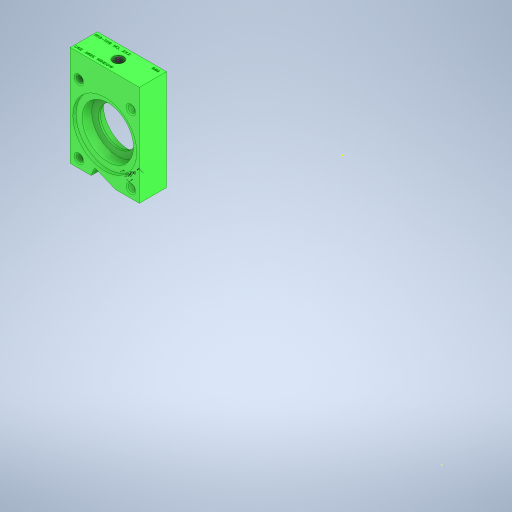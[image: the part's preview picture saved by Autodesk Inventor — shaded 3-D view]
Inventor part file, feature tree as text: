
AUTODESK INVENTOR PART (.ipt)
format: ipt  version: 2024.1 (Build 281209000, 209)  size: 907,264 bytes
history: native  units: in
note: dims shown in document units (in); Inventor stores cm internally (conversion verified against a paired STEP export)
features: hole x6, extrude x4, sketch x3, fillet x1
ambient origin geometry x8: Origin, YZ Plane, XZ Plane, XY Plane, X Axis, Y Axis, Z Axis, Center Point
bodies: Solid1 (feature_tree)
feature tree (14):
  extrude  "Extrusion1"  Depth=0.4in TaperAngle=0.0deg
  extrude  "Extrusion2"  Depth=0.0312in
  extrude  "Extrusion3"  Depth=0.0312in
  hole  "Hole1"  [1 undecoded]
  hole  "Hole2"  [1 undecoded]
  extrude  "Extrusion4"  Depth=0.0312in
  hole  "Hole5"  [1 undecoded]
  hole  "Hole6"  [1 undecoded]
  fillet  "Fillet1"  Radius=1.0in
  hole  "Hole3"  [1 undecoded]
  hole  "Hole4"  [1 undecoded]
  sketch  "Sketch1"  dims[d0=0.5in d1=0.0in d2=0.4in d3=0.0in]
  sketch  "Sketch2"  dims[d4=0.6in d5=0.0in]
  sketch  "Sketch5"  dims[d6=0.211in d7=0.25in d8=0.507in d9=0.25in d10=0.5635in d11=0.25in d12=0.0in d13=0.03in d14=0.75in d15=0.507in d16=0.25in d17=0.5635in d18=1.0in d19=0.8108in d20=0.4583in d21=0.29in d22=0.04in d23=0.75in d24=0.507in d25=0.25in d26=0.5635in d27=1.0in d28=0.8108in d29=0.213in d30=0.75in d31=0.507in d32=0.25in d33=0.5635in d34=0.25in d35=0.0in d36=0.75in d38=135.0deg d39=0.4583in d40=112.5deg d41=0.25in d42=1.0in d43=0.0in d44=0.29in d45=0.196in d46=0.211in d47=0.22in d48=0.375in d49=0.25in d50=0.5635in d51=0.22in d52=0.0in d53=0.03in d54=0.75in d55=0.375in d56=0.25in d57=0.5635in d58=0.6in d59=0.8108in d60=0.0312in]
note: 6 required parameter values undecoded (feature->parameter linkage not recoverable at this tier; creation-order binding heuristic only, values carry confidence <= 0.55)
